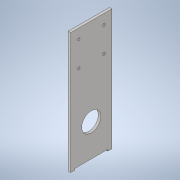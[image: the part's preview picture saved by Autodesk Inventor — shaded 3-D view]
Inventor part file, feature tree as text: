
AUTODESK INVENTOR PART (.ipt)
format: ipt  version: 2020 (Build 240168000, 168)  size: 123,904 bytes
history: native  units: mm
features: extrude x2, sketch x2
ambient origin geometry x8: Origin, YZ Plane, XZ Plane, XY Plane, X Axis, Y Axis, Z Axis, Center Point
bodies: Solid1 (feature_tree)
feature tree (4):
  extrude  "Base"  Depth=82.0mm
  extrude  "Bracket holes"  Depth=10.0mm
  sketch  "Sketch1"  dims[d0=241.0mm d1=82.0mm]
  sketch  "Sketch2"  dims[d2=38.0mm d3=41.0mm d4=174.0mm d5=66.0mm d6=3.0mm d7=8.0mm d8=5.0mm d9=0.0mm d10=5.0mm d11=20.0mm d13=50.0mm d14=20.0mm d16=50.0mm d19=19.5mm d20=10.0mm d21=0.0mm]
